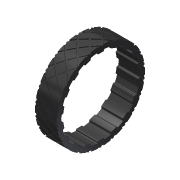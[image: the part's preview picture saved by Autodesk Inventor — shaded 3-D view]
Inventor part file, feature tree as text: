
AUTODESK INVENTOR PART (.ipt)
format: ipt  version: 2013 (Build 170138000, 138)  size: 783,360 bytes
history: native  units: in
note: dims shown in document units (in); Inventor stores cm internally (conversion verified against a paired STEP export)
features: mirror x1, imported_body x1
ambient origin geometry x8: Origin, YZ Plane, XZ Plane, XY Plane, X Axis, Y Axis, Z Axis, Center Point
feature tree (2):
  mirror  "Mirror1"
  imported_body  "Base1"
